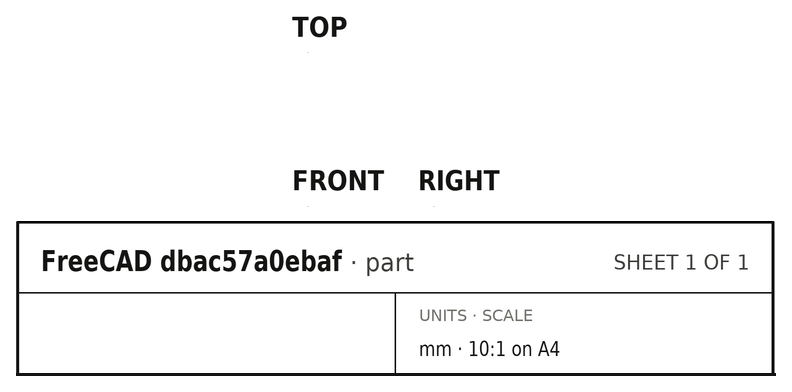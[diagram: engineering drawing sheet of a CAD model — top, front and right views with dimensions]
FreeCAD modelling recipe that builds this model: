
FCSTD DOCUMENT  (FreeCAD 0.21R33694 (Git))
Label: diffPair
License: All rights reserved
LicenseURL: http://en.wikipedia.org/wiki/All_rights_reserved
objects: Part::Part2DObjectPython×22, App::FeaturePython×10, Part::Extrusion×4, Part::Cut×2, Part::FeaturePython×2
note: 30 computed .brp shape members not serialized (recipe doc carries the construction recipe); baked Part::Feature solids carry a one-line shape summary decoded from their .brp

FEATURE [Part::Part2DObjectPython] Wire  # Draft 2D object (typed FeaturePython)
  Area = 0.0014181
  ChamferSize = 0
  Closed = true
  End = (-0.05,0,0)
  FilletRadius = 0
  Length = 0.221006
  MakeFace = true
  Placement = pos=(-0.15,0,0) rot=(0,0,1;0rad)
  Points = (4) [(0,0,0),(0.00545955,0.015,0),(0.0945402,0.015,0),(0.1,-6.12323e-18,0)]
  Start = (-0.15,0,0)
  Subdivisions = 0
FEATURE [Part::Part2DObjectPython] Wire001  # Draft 2D object (typed FeaturePython)
  Area = 0.0014181
  ChamferSize = 0
  Closed = true
  End = (0.15,0,0)
  FilletRadius = 0
  Length = 0.221006
  MakeFace = true
  Placement = pos=(0.05,0,0) rot=(0,0,1;0rad)
  Points = (4) [(0,0,0),(0.00545955,0.015,0),(0.0945402,0.015,0),(0.1,-6.12323e-18,0)]
  Start = (0.05,0,0)
  Subdivisions = 0
FEATURE [Part::Part2DObjectPython] Rectangle  # Draft 2D object (typed FeaturePython)
  Area = 0.13
  ChamferSize = 0
  Columns = 1
  FilletRadius = 0
  Height = 0.1
  Length = 1.3
  MakeFace = true
  Placement = pos=(-0.65,-0.1,0) rot=(0,0,1;0rad)
  Rows = 1
FEATURE [Part::Part2DObjectPython] Rectangle001  # Draft 2D object (typed FeaturePython)
  Area = 0.13
  ChamferSize = 0
  Columns = 1
  FilletRadius = 0
  Height = 0.1
  Length = 1.3
  MakeFace = true
  Placement = pos=(-0.65,0,0) rot=(0,0,1;0rad)
  Rows = 1
FEATURE [Part::Part2DObjectPython] Clone2D  label="Wire (2D)"  # Draft 2D object (typed FeaturePython)
  Fuse = false
  Objects = -> [Wire]
  Placement = pos=(-0.15,0,0) rot=(0,0,1;0rad)
  Scale = (1,1,1)
FEATURE [Part::Part2DObjectPython] Clone2D001  label="Wire001 (2D)"  # Draft 2D object (typed FeaturePython)
  Fuse = false
  Objects = -> [Wire001]
  Placement = pos=(0.05,0,0) rot=(0,0,1;0rad)
  Scale = (1,1,1)
FEATURE [Part::Part2DObjectPython] Clone2D002  label="Rectangle (2D)"  # Draft 2D object (typed FeaturePython)
  Fuse = false
  Objects = -> [Rectangle]
  Placement = pos=(-0.65,-0.1,0) rot=(0,0,1;0rad)
  Scale = (1,1,1)
FEATURE [Part::Part2DObjectPython] Clone2D003  label="Rectangle001 (2D)"  # Draft 2D object (typed FeaturePython)
  Fuse = false
  Objects = -> [Rectangle001]
  Placement = pos=(-0.65,0,0) rot=(0,0,1;0rad)
  Scale = (1,1,1)
FEATURE [Part::Part2DObjectPython] Clone2D004  label="Wire (2D)001"  # Draft 2D object (typed FeaturePython)
  Fuse = false
  Objects = -> [Wire]
  Placement = pos=(-0.15,0,0) rot=(0,0,1;0rad)
  Scale = (1,1,1)
FEATURE [Part::Part2DObjectPython] Clone2D005  label="Wire001 (2D)001"  # Draft 2D object (typed FeaturePython)
  Fuse = false
  Objects = -> [Wire001]
  Placement = pos=(0.05,0,0) rot=(0,0,1;0rad)
  Scale = (1,1,1)
FEATURE [Part::Part2DObjectPython] Clone2D006  label="Rectangle (2D)001"  # Draft 2D object (typed FeaturePython)
  Fuse = false
  Objects = -> [Rectangle]
  Placement = pos=(-0.65,-0.1,0) rot=(0,0,1;0rad)
  Scale = (1,1,1)
FEATURE [Part::Part2DObjectPython] Clone2D007  label="Rectangle001 (2D)001"  # Draft 2D object (typed FeaturePython)
  Fuse = false
  Objects = -> [Rectangle001]
  Placement = pos=(-0.65,0,0) rot=(0,0,1;0rad)
  Scale = (1,1,1)
FEATURE [Part::Extrusion] Extrude004
  Base = -> Clone2D
  Dir = (0,0,1)
  DirMode = 2
  FaceMakerClass = Part::FaceMakerBullseye
  LengthFwd = 2
  LengthRev = 0
  Solid = false
  Symmetric = false
FEATURE [Part::Extrusion] Extrude005
  Base = -> Clone2D001
  Dir = (0,0,1)
  DirMode = 2
  FaceMakerClass = Part::FaceMakerBullseye
  LengthFwd = 2
  LengthRev = 0
  Solid = false
  Symmetric = false
FEATURE [Part::Extrusion] Extrude006
  Base = -> Clone2D002
  Dir = (0,0,1)
  DirMode = 2
  FaceMakerClass = Part::FaceMakerBullseye
  LengthFwd = 2
  LengthRev = 0
  Solid = false
  Symmetric = false
FEATURE [Part::Extrusion] Extrude007
  Base = -> Clone2D003
  Dir = (0,0,1)
  DirMode = 2
  FaceMakerClass = Part::FaceMakerBullseye
  LengthFwd = 2
  LengthRev = 0
  Solid = false
  Symmetric = false
FEATURE [Part::Cut] Cut002
  Base = -> Extrude007
  Tool = -> Extrude004
FEATURE [Part::Cut] Cut003
  Base = -> Cut002
  Tool = -> Extrude005
FEATURE [App::FeaturePython] Text010  label="_Sin(PV){port1}"  # WARN: FeaturePython — macro-defined, semantics opaque (R4)
  Placement = pos=(5.00075,-5.09743,10) rot=(0,0,1;0rad)
  Text = .
FEATURE [App::FeaturePython] Text011  label="_Sout(PV){port2}"  # WARN: FeaturePython — macro-defined, semantics opaque (R4)
  Placement = pos=(5.00075,-5.09743,10) rot=(0,0,1;0rad)
  Text = .
FEATURE [App::FeaturePython] Text012  label="_Min(1,voltage,comm_in,0.5){v11,v12}"  # WARN: FeaturePython — macro-defined, semantics opaque (R4)
  Placement = pos=(5.00075,-5.09743,10) rot=(0,0,1;0rad)
  Text = .
FEATURE [App::FeaturePython] Text013  label="_Min(1,current,comm_in){i11,i12}"  # WARN: FeaturePython — macro-defined, semantics opaque (R4)
  Placement = pos=(5.00075,-5.09743,10) rot=(0,0,1;0rad)
  Text = .
FEATURE [App::FeaturePython] Text014  label="_Min(2,voltage,diff_in){v11,-v12}"  # WARN: FeaturePython — macro-defined, semantics opaque (R4)
  Placement = pos=(5.00075,-5.09743,10) rot=(0,0,1;0rad)
  Text = .
FEATURE [App::FeaturePython] Text015  label="_Min(2,current,diff_in,0.5){i11,-i12}"  # WARN: FeaturePython — macro-defined, semantics opaque (R4)
  Placement = pos=(5.00075,-5.09743,10) rot=(0,0,1;0rad)
  Text = .
FEATURE [App::FeaturePython] Text016  label="_Mout(3,voltage,comm_out,0.5){v21,v22}"  # WARN: FeaturePython — macro-defined, semantics opaque (R4)
  Placement = pos=(5.00075,-5.09743,10) rot=(0,0,1;0rad)
  Text = .
FEATURE [App::FeaturePython] Text017  label="_Mout(3,current,comm_out){i21,i22}"  # WARN: FeaturePython — macro-defined, semantics opaque (R4)
  Placement = pos=(5.00075,-5.09743,10) rot=(0,0,1;0rad)
  Text = .
FEATURE [App::FeaturePython] Text018  label="_Mout(4,voltage,diff_out){v21,-v22}"  # WARN: FeaturePython — macro-defined, semantics opaque (R4)
  Placement = pos=(5.00075,-5.09743,10) rot=(0,0,1;0rad)
  Text = .
FEATURE [App::FeaturePython] Text019  label="_Mout(4,current,diff_out,0.5){i21,-i22}"  # WARN: FeaturePython — macro-defined, semantics opaque (R4)
  Placement = pos=(5.00075,-5.09743,10) rot=(0,0,1;0rad)
  Text = .
FEATURE [Part::Part2DObjectPython] Wire006  label="_Pi22"  # Draft 2D object (typed FeaturePython)
  Area = 1.4181e-09
  ChamferSize = 0
  Closed = true
  End = (5e-05,-0.0999,4.995)
  FilletRadius = 0
  Length = 0.000221006
  MakeFace = true
  Placement = pos=(0.00015,-0.0999,4.995) rot=(0.707107,0.707107,0;3.14159rad)
  Points = (4) [(0,0,0),(1.5e-05,-5.45983e-06,0),(1.5e-05,-9.45404e-05,0),(0,-0.0001,0)]
  Start = (0.00015,-0.0999,4.995)
  Subdivisions = 0
FEATURE [Part::Part2DObjectPython] Wire007  label="_Pi21"  # Draft 2D object (typed FeaturePython)
  Area = 1.4181e-09
  ChamferSize = 0
  Closed = true
  End = (-0.00015,-0.0999,4.995)
  FilletRadius = 0
  Length = 0.000221006
  MakeFace = true
  Placement = pos=(-5e-05,-0.0999,4.995) rot=(0.707107,0.707107,0;3.14159rad)
  Points = (4) [(0,0,0),(1.5e-05,-5.45983e-06,0),(1.5e-05,-9.45404e-05,0),(0,-0.0001,0)]
  Start = (-5e-05,-0.0999,4.995)
  Subdivisions = 0
FEATURE [Part::Part2DObjectPython] Wire008  label="_Pi11"  # Draft 2D object (typed FeaturePython)
  Area = 1.4181e-09
  ChamferSize = 0
  Closed = true
  End = (-5e-05,-0.0999,4.997)
  FilletRadius = 0
  Length = 0.000221006
  MakeFace = true
  Placement = pos=(-0.00015,-0.0999,4.997) rot=(0,0,1;0rad)
  Points = (4) [(0,0,0),(5.45955e-06,1.5e-05,0),(9.45402e-05,1.5e-05,0),(0.0001,0,0)]
  Start = (-0.00015,-0.0999,4.997)
  Subdivisions = 0
FEATURE [Part::Part2DObjectPython] Wire009  label="_Pi12"  # Draft 2D object (typed FeaturePython)
  Area = 1.4181e-09
  ChamferSize = 0
  Closed = true
  End = (0.00015,-0.0999,4.997)
  FilletRadius = 0
  Length = 0.000221006
  MakeFace = true
  Placement = pos=(5e-05,-0.0999,4.997) rot=(0,0,1;0rad)
  Points = (4) [(0,0,0),(5.45955e-06,1.5e-05,0),(9.45402e-05,1.5e-05,0),(0.0001,0,0)]
  Start = (5e-05,-0.0999,4.997)
  Subdivisions = 0
FEATURE [Part::Part2DObjectPython] Rectangle013  label="_Pport1"  # Draft 2D object (typed FeaturePython)
  Area = 2.6e-07
  ChamferSize = 0
  Columns = 1
  FilletRadius = 0
  Height = 0.0002
  Length = 0.0013
  MakeFace = true
  Placement = pos=(-0.00065,-0.1,4.997) rot=(0,0,1;0rad)
  Rows = 1
FEATURE [Part::Part2DObjectPython] Line  label="_Pv11"  # Draft 2D object (typed FeaturePython)
  Area = 0
  ChamferSize = 0
  Closed = false
  End = (-0.0001,-0.0999,4.997)
  FilletRadius = 0
  Length = 0.0001
  MakeFace = true
  Placement = pos=(0,-0.1,4.997) rot=(0,0,1;0rad)
  Points = (2) [(-0.0001,0,0),(-0.0001,0.0001,0)]
  Start = (-0.0001,-0.1,4.997)
  Subdivisions = 0
FEATURE [Part::Part2DObjectPython] Line004  label="_Pv12"  # Draft 2D object (typed FeaturePython)
  Area = 0
  ChamferSize = 0
  Closed = false
  End = (0.0001,-0.0999,4.997)
  FilletRadius = 0
  Length = 0.0001
  MakeFace = true
  Placement = pos=(0,-0.1,4.997) rot=(0,0,1;0rad)
  Points = (2) [(0.0001,0,0),(0.0001,0.0001,0)]
  Start = (0.0001,-0.1,4.997)
  Subdivisions = 0
FEATURE [Part::Part2DObjectPython] Rectangle014  label="_Pport2"  # Draft 2D object (typed FeaturePython)
  Area = 2.6e-07
  ChamferSize = 0
  Columns = 1
  FilletRadius = 0
  Height = 0.0013
  Length = 0.0002
  MakeFace = true
  Placement = pos=(-0.00065,-0.1,4.995) rot=(0.707107,0.707107,0;3.14159rad)
  Rows = 1
FEATURE [Part::Part2DObjectPython] Line005  label="_Pv21"  # Draft 2D object (typed FeaturePython)
  Area = 0
  ChamferSize = 0
  Closed = false
  End = (-0.0001,-0.0999,4.995)
  FilletRadius = 0
  Length = 0.0001
  MakeFace = true
  Placement = pos=(0,-0.1,4.995) rot=(0.707107,0.707107,0;3.14159rad)
  Points = (2) [(1.38778e-17,-0.0001,0),(0.0001,-0.0001,0)]
  Start = (-0.0001,-0.1,4.995)
  Subdivisions = 0
FEATURE [Part::Part2DObjectPython] Line006  label="_Pv22"  # Draft 2D object (typed FeaturePython)
  Area = 0
  ChamferSize = 0
  Closed = false
  End = (0.0001,-0.0999,4.995)
  FilletRadius = 0
  Length = 0.0001
  MakeFace = true
  Placement = pos=(0,-0.1,4.995) rot=(0.707107,0.707107,0;3.14159rad)
  Points = (2) [(1.38778e-17,0.0001,0),(0.0001,0.0001,0)]
  Start = (0.0001,-0.1,4.995)
  Subdivisions = 0
FEATURE [Part::FeaturePython] BooleanFragments  # WARN: FeaturePython — macro-defined, semantics opaque (R4)
  Mode = 0
  Objects = -> [Extrude006,Cut003]
  Tolerance = 0
FEATURE [Part::FeaturePython] Clone  label="scaled"  # Draft clone (typed FeaturePython)
  AttacherType = Attacher::AttachEngine3D
  Fuse = false
  Objects = -> [BooleanFragments]
  Placement = pos=(0,-0.0999,4.995) rot=(0,0,1;0rad)
  Scale = (0.001,0.001,0.001)
